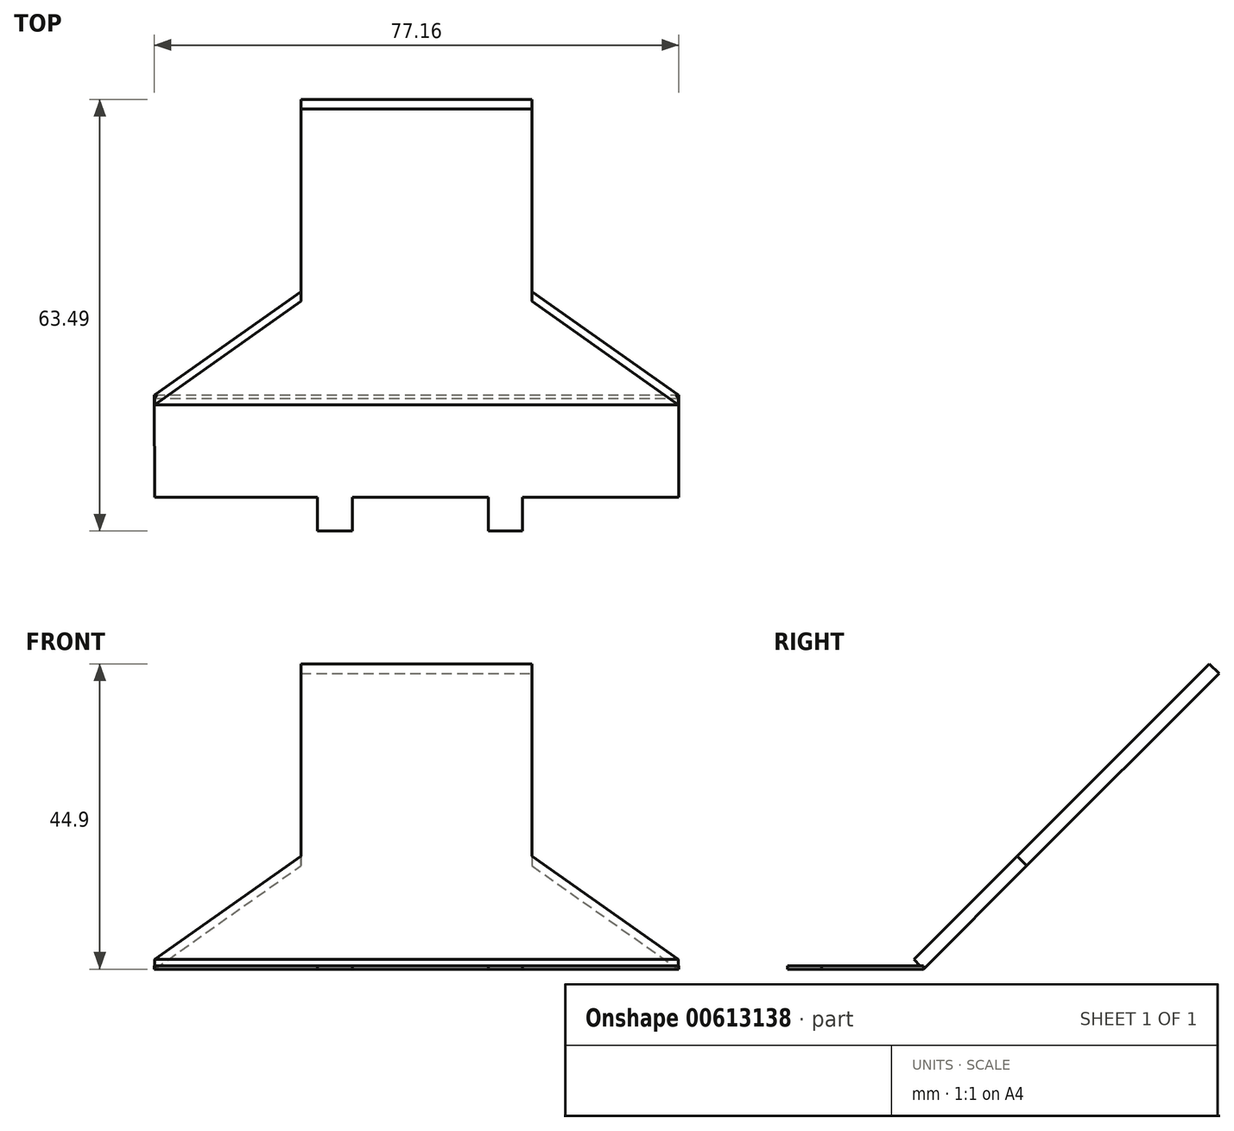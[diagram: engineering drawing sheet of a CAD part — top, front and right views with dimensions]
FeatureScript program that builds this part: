
annotation { "Feature Type Name" : "Feature", "Feature Type Description" : "" }
export const myFeature = defineFeature(function(context is Context, id is Id, definition is map)
    precondition{}
    {
        {
            var Q0;
            Q0=qCreatedBy(makeId("Top.planeOp"),FACE);
            var sketch = newSketch(context, id + "F0", { "sketchPlane" : qUnion([Q0])});
            skLineSegment(sketch, "E0", {"start": v(-36.54, 0) * mm, "end": v(40.62, 0) * mm});
            skLineSegment(sketch, "E1", {"start": v(40.62, 0) * mm, "end": v(40.62, -15) * mm});
            skLineSegment(sketch, "E2", {"start": v(40.62, -15) * mm, "end": v(17.62, -15) * mm});
            skLineSegment(sketch, "E3", {"start": v(17.62, -15) * mm, "end": v(17.62, -20) * mm});
            skLineSegment(sketch, "E4", {"start": v(17.62, -20) * mm, "end": v(12.62, -20) * mm});
            skLineSegment(sketch, "E5", {"start": v(12.62, -20) * mm, "end": v(12.62, -15) * mm});
            skLineSegment(sketch, "E6", {"start": v(12.62, -15) * mm, "end": v(-7.38, -15) * mm});
            skLineSegment(sketch, "E7", {"start": v(-7.38, -15) * mm, "end": v(-7.38, -20) * mm});
            skLineSegment(sketch, "E8", {"start": v(-7.38, -20) * mm, "end": v(-12.53, -20) * mm});
            skLineSegment(sketch, "E9", {"start": v(-12.53, -20) * mm, "end": v(-12.53, -15) * mm});
            skLineSegment(sketch, "E10", {"start": v(-12.53, -15) * mm, "end": v(-36.46, -15) * mm});
            skPoint(sketch, "E11", {"position": v(40.62, 0) * mm});
            skLineSegment(sketch, "E12", {"start": v(-36.54, 0) * mm, "end": v(-36.46, -15) * mm});
            skSolve(sketch);
        }
        {
            var Q0;
            Q0=qCreatedBy(makeId("Top.planeOp"),FACE);
            var Q1;
            Q1=qCreatedBy(makeId("Front.planeOp"),FACE);
            cPlane(context, id + "F1", {"entities" : qUnion([Q0, Q1]), "cplaneType" : CPlaneType.MID_PLANE, "offset" : 25 * mm, "flipAlignment" : true, "width" : 150 * mm, "height" : 150 * mm});
        }
        {
            var Q0;
            Q0=qCreatedBy(id+"F1.planeOp",FACE);
            var sketch = newSketch(context, id + "F2", { "sketchPlane" : qUnion([Q0])});
            skLineSegment(sketch, "E13", {"start": v(-36.45, 0) * mm, "end": v(-14.95, 21.5) * mm});
            skLineSegment(sketch, "E14", {"start": v(-14.95, 21.5) * mm, "end": v(-14.95, 61.5) * mm});
            skLineSegment(sketch, "E15", {"start": v(-14.95, 61.5) * mm, "end": v(19.05, 61.5) * mm});
            skLineSegment(sketch, "E16", {"start": v(19.05, 61.5) * mm, "end": v(19.05, 21.5) * mm});
            skLineSegment(sketch, "E17", {"start": v(19.05, 21.5) * mm, "end": v(40.55, 0) * mm});
            skLineSegment(sketch, "E18", {"start": v(-36.45, 0) * mm, "end": v(40.55, 0) * mm});
            skSolve(sketch);
        }
        {
            var Q0;
            Q0 = qSketchRegion(id + "F2", true);
            extrude(context, id + "F3", {"entities" : qUnion([Q0]), "depth" : 2 * mm, "offsetDistance" : 25 * mm});
        }
        {
            var Q0;
            Q0=makeQuery(id+"F0.imprint","IMPRINT",FACE,{"disambiguationData":[TD([[makeQuery(id+"F0.imprint","IMPRINT",EDGE,{"derivedFrom":sQuery(id+"F0.wireOp",EDGE,"E0")}),-1.0]])]});
            extrude(context, id + "F4", {"entities" : qUnion([Q0]), "operationType" : NewBodyOperationType.ADD, "depth" : 0.5 * mm, "offsetDistance" : 25 * mm});
        }
    });
